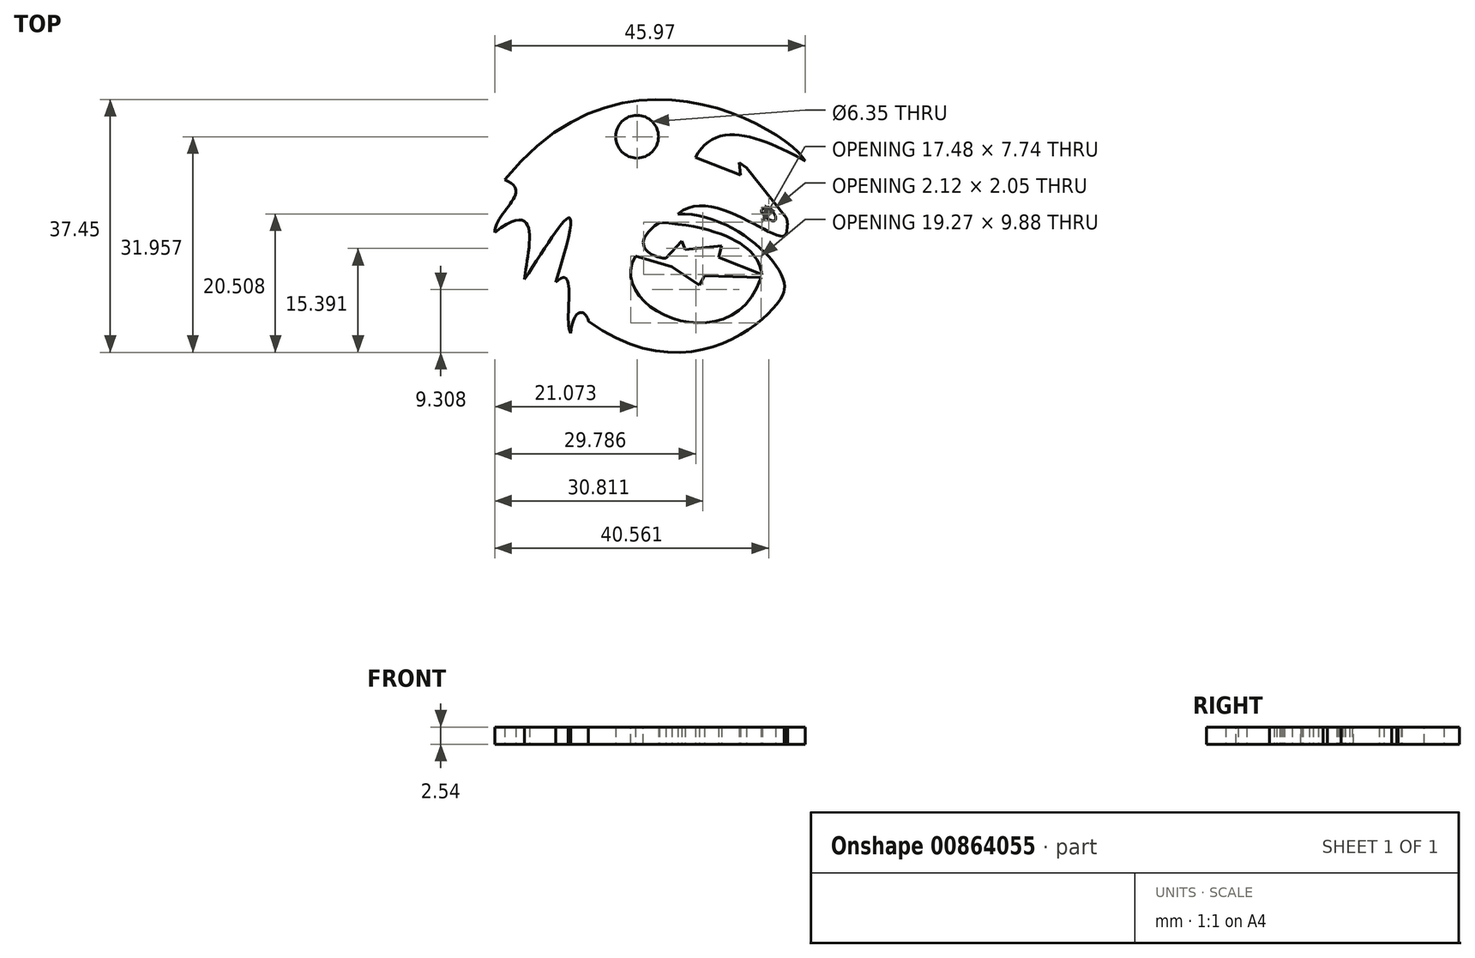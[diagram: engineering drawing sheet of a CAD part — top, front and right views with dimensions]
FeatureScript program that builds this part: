
annotation { "Feature Type Name" : "Feature", "Feature Type Description" : "" }
export const myFeature = defineFeature(function(context is Context, id is Id, definition is map)
    precondition{}
    {
        {
            var Q0;
            Q0=qCreatedBy(makeId("Top.planeOp"),FACE);
            var sketch = newSketch(context, id + "F0", { "sketchPlane" : qUnion([Q0])});
            skFitSpline(sketch, "E0", {"points": [v(16.92, 11.13) * mm, v(0.67, 11.68) * mm], "startDerivative": vector(-18.9, 10.56) * mm, "endDerivative": vector(-9, -17.43) * mm});
            skFitSpline(sketch, "E1", {"points": [v(16.92, 11.13) * mm, v(-27.56, 8.37) * mm], "startDerivative": vector(-6.16, 12.35) * mm, "endDerivative": vector(-53.82, -67.38) * mm});
            skFitSpline(sketch, "E2", {"points": [v(-27.56, 8.37) * mm, v(-29.05, 0.54) * mm], "startDerivative": vector(13.26, -5.3) * mm, "endDerivative": vector(0, -9.34) * mm});
            skFitSpline(sketch, "E3", {"points": [v(-29.05, 0.54) * mm, v(-24.64, -6.37) * mm], "startDerivative": vector(22.84, 17.78) * mm, "endDerivative": vector(-0.58, -9.07) * mm});
            skFitSpline(sketch, "E4", {"points": [v(-20.03, -6.85) * mm, v(-24.64, -6.37) * mm], "startDerivative": vector(16.2, 51.82) * mm, "endDerivative": vector(-13.53, -20.15) * mm});
            skFitSpline(sketch, "E5", {"points": [v(-20.03, -6.85) * mm, v(-17.83, -14.37) * mm], "startDerivative": vector(10.36, 9.76) * mm, "endDerivative": vector(3.27, -6.22) * mm});
            skFitSpline(sketch, "E6", {"points": [v(-15.17, -12.57) * mm, v(13.85, -7.93) * mm], "startDerivative": vector(48.33, -35.27) * mm, "endDerivative": vector(-0.16, 7.36) * mm});
            skFitSpline(sketch, "E7", {"points": [v(14.18, 0.63) * mm, v(-1.9, 3.3) * mm], "startDerivative": vector(-0.99, -9.72) * mm, "endDerivative": vector(-15.96, -14.04) * mm});
            skFitSpline(sketch, "E8", {"points": [v(-4.66, 2.04) * mm, v(10.5, -5.7) * mm], "startDerivative": vector(32.9, -2.16) * mm, "endDerivative": vector(0.54, -9.77) * mm});
            skFitSpline(sketch, "E9", {"points": [v(-4.66, 2.04) * mm, v(-3.7, -3.26) * mm], "startDerivative": vector(-16.9, -11.8) * mm, "endDerivative": vector(1.66, 0.71) * mm});
            skLineSegment(sketch, "E10", {"start": v(-3.7, -3.26) * mm, "end": v(-1.37, -0.7) * mm});
            skLineSegment(sketch, "E11", {"start": v(-1.37, -0.7) * mm, "end": v(-0.83, -2) * mm});
            skLineSegment(sketch, "E12", {"start": v(-0.83, -2) * mm, "end": v(4.55, -1.42) * mm});
            skLineSegment(sketch, "E13", {"start": v(4.55, -1.42) * mm, "end": v(4.14, -3.16) * mm});
            skLineSegment(sketch, "E14", {"start": v(4.14, -3.16) * mm, "end": v(10.5, -5.7) * mm});
            skFitSpline(sketch, "E15", {"points": [v(13.85, -7.93) * mm, v(-1.9, 3.3) * mm], "startDerivative": vector(1.87, 11) * mm, "endDerivative": vector(-23.56, -0.98) * mm});
            skLineSegment(sketch, "E16", {"start": v(2.01, -5.9) * mm, "end": v(1.27, -7.24) * mm});
            skLineSegment(sketch, "E17", {"start": v(1.27, -7.24) * mm, "end": v(-2.8, -4.55) * mm});
            skLineSegment(sketch, "E18", {"start": v(-2.8, -4.55) * mm, "end": v(-8.23, -2.97) * mm});
            skFitSpline(sketch, "E19", {"points": [v(-8.23, -2.97) * mm, v(10.5, -5.7) * mm], "startDerivative": vector(-13.73, -24.32) * mm, "endDerivative": vector(11.36, 40.13) * mm});
            skLineSegment(sketch, "E20", {"start": v(8.25, 10.15) * mm, "end": v(14.13, 2.7) * mm});
            skLineSegment(sketch, "E21", {"start": v(14.29, 1.47) * mm, "end": v(14.18, 0.63) * mm});
            skFitSpline(sketch, "E22", {"points": [v(12.57, 2.93) * mm, v(10.56, 3.99) * mm], "startDerivative": vector(0.45, -5.48) * mm, "endDerivative": vector(2.1, 1.3) * mm});
            skFitSpline(sketch, "E23", {"points": [v(10.56, 3.99) * mm, v(12.57, 2.93) * mm], "startDerivative": vector(4.15, 2.68) * mm, "endDerivative": vector(1.89, -2.47) * mm});
            skFitSpline(sketch, "E24", {"points": [v(-17.83, -14.37) * mm, v(-15.17, -12.57) * mm], "startDerivative": vector(1.83, 13.24) * mm, "endDerivative": vector(0.84, -4.1) * mm});
            skArc(sketch, "E25.filletArc", {"start": v(14.29, 1.47) * mm, "mid": v(14.29, 2.1) * mm, "end": v(14.13, 2.7) * mm});
            skLineSegment(sketch, "E26", {"start": v(8.25, 10.15) * mm, "end": v(7.17, 10.92) * mm});
            skLineSegment(sketch, "E27", {"start": v(7.17, 10.92) * mm, "end": v(7.35, 9.04) * mm});
            skLineSegment(sketch, "E28", {"start": v(7.35, 9.04) * mm, "end": v(0.67, 11.68) * mm});
            skLineSegment(sketch, "E29", {"start": v(2.01, -5.9) * mm, "end": v(10.37, -6.12) * mm});
            skPoint(sketch, "E30", {"position": v(-7.98, 14.74) * mm});
            skSolve(sketch);
        }
        {
            var Q0;
            Q0=makeQuery(id+"F0.imprint","IMPRINT",FACE,{"disambiguationData":[TD([[makeQuery(id+"F0.imprint","IMPRINT",EDGE,{"derivedFrom":sQuery(id+"F0.wireOp",EDGE,"E0")}),-1.0]])]});
            extrude(context, id + "F1", {"entities" : qUnion([Q0]), "depth" : 2.54 * mm, "offsetDistance" : 25.4 * mm});
        }
        {
            var Q0;
            Q0=sQuery(id+"F0.wireOp",VERTEX,"E30");
            var Q1;
            Q1=makeQuery(id+"F1.opExtrude","SWEPT_BODY",BODY,{"disambiguationData":[OSD([sQuery(id+"F0.wireOp",EDGE,"E0"),sQuery(id+"F0.wireOp",EDGE,"E1"),sQuery(id+"F0.wireOp",EDGE,"E2"),sQuery(id+"F0.wireOp",EDGE,"E3"),sQuery(id+"F0.wireOp",EDGE,"E4"),sQuery(id+"F0.wireOp",EDGE,"E5"),sQuery(id+"F0.wireOp",EDGE,"E6"),sQuery(id+"F0.wireOp",EDGE,"E7"),sQuery(id+"F0.wireOp",EDGE,"E8"),sQuery(id+"F0.wireOp",EDGE,"E9"),sQuery(id+"F0.wireOp",EDGE,"E10"),sQuery(id+"F0.wireOp",EDGE,"E11"),sQuery(id+"F0.wireOp",EDGE,"E12"),sQuery(id+"F0.wireOp",EDGE,"E13"),sQuery(id+"F0.wireOp",EDGE,"E14"),sQuery(id+"F0.wireOp",EDGE,"E15"),sQuery(id+"F0.wireOp",EDGE,"E16"),sQuery(id+"F0.wireOp",EDGE,"E17"),sQuery(id+"F0.wireOp",EDGE,"E18"),sQuery(id+"F0.wireOp",EDGE,"E19"),sQuery(id+"F0.wireOp",EDGE,"E20"),sQuery(id+"F0.wireOp",EDGE,"E21"),sQuery(id+"F0.wireOp",EDGE,"E22"),sQuery(id+"F0.wireOp",EDGE,"E23"),sQuery(id+"F0.wireOp",EDGE,"E24"),sQuery(id+"F0.wireOp",EDGE,"E25.filletArc"),sQuery(id+"F0.wireOp",EDGE,"E26"),sQuery(id+"F0.wireOp",EDGE,"E27"),sQuery(id+"F0.wireOp",EDGE,"E28"),sQuery(id+"F0.wireOp",EDGE,"E29")])]});
            hole(context, id + "F2", {"style" : HoleStyle.SIMPLE, "endStyle" : HoleEndStyle.THROUGH, "oppositeDirection" : true, "holeDiameter" : 6.35 * mm, "majorDiameter" : 6.35 * mm, "isTappedThrough" : true, "tappedDepth" : 12.7 * mm, "tapClearance" : 3, "locations" : qUnion([Q0]), "scope" : qUnion([Q1])});
        }
    });
